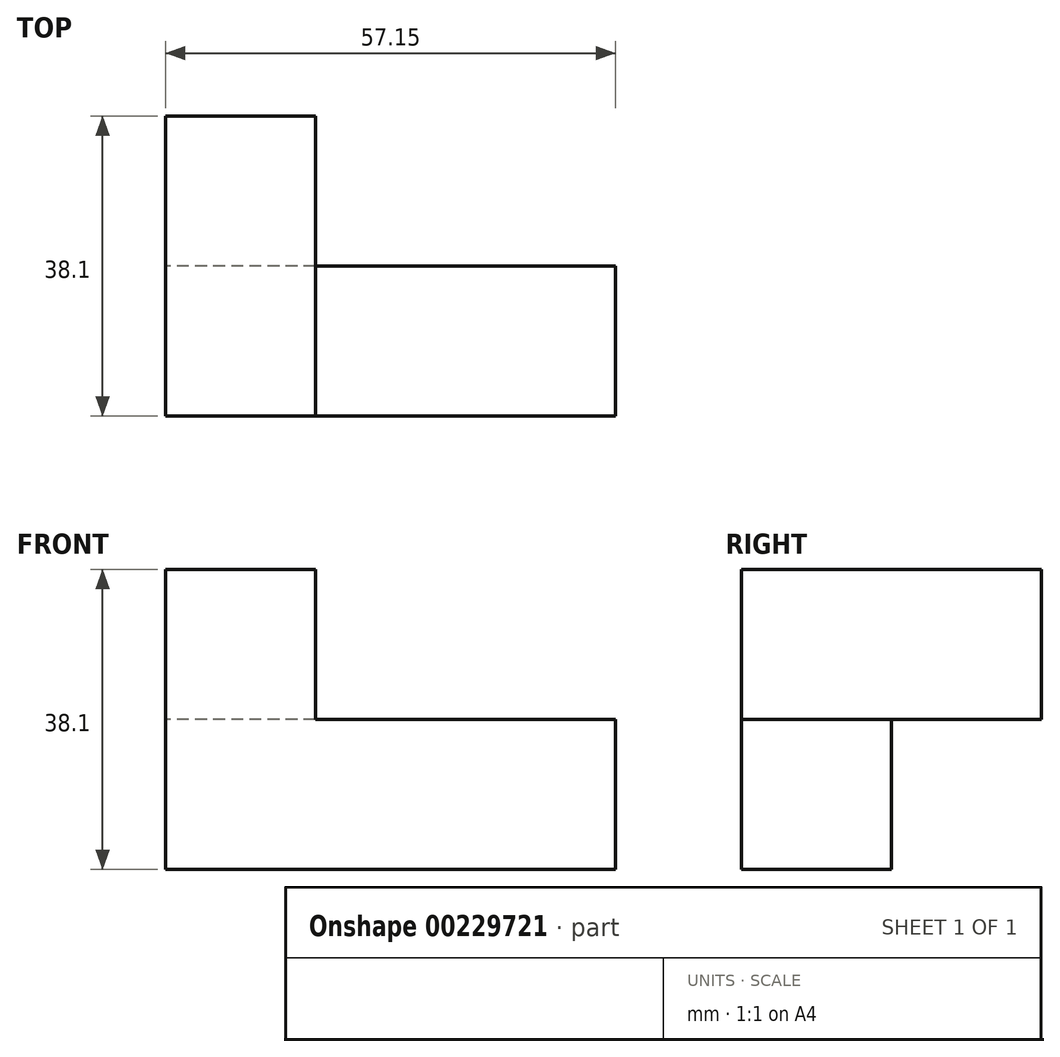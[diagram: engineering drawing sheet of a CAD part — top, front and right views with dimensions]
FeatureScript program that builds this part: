
annotation { "Feature Type Name" : "Feature", "Feature Type Description" : "" }
export const myFeature = defineFeature(function(context is Context, id is Id, definition is map)
    precondition{}
    {
        {
            var Q0;
            Q0=qCreatedBy(makeId("Front.planeOp"),FACE);
            var sketch = newSketch(context, id + "F0", { "sketchPlane" : qUnion([Q0])});
            skLineSegment(sketch, "E0.bottom", {"start": v(-25.45, 5.8) * mm, "end": v(31.7, 5.8) * mm});
            skLineSegment(sketch, "E0.top", {"start": v(-25.45, -13.26) * mm, "end": v(31.7, -13.26) * mm});
            skLineSegment(sketch, "E0.left", {"start": v(-25.45, 5.8) * mm, "end": v(-25.45, -13.26) * mm});
            skLineSegment(sketch, "E0.right", {"start": v(31.7, 5.8) * mm, "end": v(31.7, -13.26) * mm});
            skSolve(sketch);
        }
        {
            var Q0;
            Q0=makeQuery(id+"F0.imprint","IMPRINT",FACE,{"disambiguationData":[TD([[makeQuery(id+"F0.imprint","IMPRINT",EDGE,{"derivedFrom":sQuery(id+"F0.wireOp",EDGE,"E0.bottom")}),-1.0]])]});
            extrude(context, id + "F1", {"entities" : qUnion([Q0]), "depth" : 19.05 * mm});
        }
        {
            var Q0;
            Q0=makeQuery(id+"F1.opExtrude","SWEPT_FACE",FACE,{"disambiguationData":[OSD([sQuery(id+"F0.wireOp",EDGE,"E0.bottom")])]});
            var sketch = newSketch(context, id + "F2", { "sketchPlane" : qUnion([Q0])});
            skLineSegment(sketch, "E1.bottom", {"start": v(-25.45, -19.05) * mm, "end": v(-6.4, -19.05) * mm});
            skLineSegment(sketch, "E1.top", {"start": v(-25.45, 19.05) * mm, "end": v(-6.4, 19.05) * mm});
            skLineSegment(sketch, "E1.left", {"start": v(-25.45, -19.05) * mm, "end": v(-25.45, 19.05) * mm});
            skLineSegment(sketch, "E1.right", {"start": v(-6.4, -19.05) * mm, "end": v(-6.4, 19.05) * mm});
            skSolve(sketch);
        }
        {
            var Q0;
            {var subQ0=sQuery(id+"F2.wireOp",EDGE,"E1.bottom");Q0=makeQuery(id+"F2.imprint","IMPRINT",FACE,{"disambiguationData":[TD([[makeQuery(id+"F2.imprint","IMPRINT",EDGE,{"derivedFrom":subQ0}),1.0]])]});}
            extrude(context, id + "F3", {"entities" : qUnion([Q0]), "operationType" : NewBodyOperationType.ADD, "depth" : 19.05 * mm});
        }
        {
            var Q0;
            {var subQ0=sQuery(id+"F0.wireOp",EDGE,"E0.bottom");Q0=makeQuery(id+"F3.boolean.opBoolean","MERGE",FACE,{"derivedFrom":[makeQuery(id+"F1.opExtrude","CAP_FACE",FACE,{"disambiguationData":[OSD([subQ0,sQuery(id+"F0.wireOp",EDGE,"E0.top"),sQuery(id+"F0.wireOp",EDGE,"E0.left"),sQuery(id+"F0.wireOp",EDGE,"E0.right")])],"isStart":true}),makeQuery(id+"F3.opExtrude","SWEPT_FACE",FACE,{"disambiguationData":[OSD([subQ0])]})]});}
            var sketch = newSketch(context, id + "F4", { "sketchPlane" : qUnion([Q0])});
            skLineSegment(sketch, "E2.bottom", {"start": v(6.4, 24.84) * mm, "end": v(25.45, 24.84) * mm});
            skLineSegment(sketch, "E2.top", {"start": v(6.4, 5.8) * mm, "end": v(25.45, 5.8) * mm});
            skLineSegment(sketch, "E2.left", {"start": v(6.4, 24.84) * mm, "end": v(6.4, 5.8) * mm});
            skLineSegment(sketch, "E2.right", {"start": v(25.45, 24.84) * mm, "end": v(25.45, 5.8) * mm});
            skSolve(sketch);
        }
        {
            var Q0;
            Q0=makeQuery(id+"F4.imprint","IMPRINT",FACE,{"disambiguationData":[TD([[makeQuery(id+"F4.imprint","IMPRINT",EDGE,{"derivedFrom":sQuery(id+"F4.wireOp",EDGE,"E2.bottom")}),1.0]])]});
            extrude(context, id + "F5", {"entities" : qUnion([Q0]), "operationType" : NewBodyOperationType.ADD, "depth" : 19.05 * mm});
        }
    });
